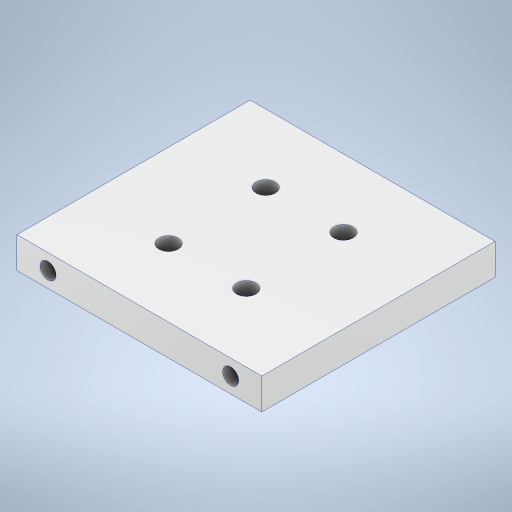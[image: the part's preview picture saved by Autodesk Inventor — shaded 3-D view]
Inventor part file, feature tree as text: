
AUTODESK INVENTOR PART (.ipt)
format: ipt  version: 2023 (Build 270158000, 158)  size: 278,016 bytes
history: native  units: mm
features: sketch x4, hole x3, other x3, extrude x1
ambient origin geometry x8: Origin, YZ Plane, XZ Plane, XY Plane, X Axis, Y Axis, Z Axis, Center Point
bodies: Body1 (feature_tree)
feature tree (11):
  extrude  "Extrusion2"  Depth=63.0mm
  hole  "Hole3"  [1 undecoded]
  hole  "Hole4"  [1 undecoded]
  hole  "Hole5"  [1 undecoded]
  sketch  "Sketch5"  dims[d43=53.25mm d68=63.0mm]
  sketch  "Sketch6"  dims[d69=60.0mm d70=8.0mm d71=0.0mm]
  sketch  "Sketch7"  dims[d72=20.0mm d74=25.0mm d75=20.0mm d77=20.0mm d80=63.0mm]
  sketch  "Sketch8"  dims[d81=60.0mm d82=21.5mm d83=17.5mm d84=5.0mm d85=6.0mm d86=4.0mm d87=2.0mm d88=90.0deg d89=5.0mm d90=20.594885mm d91=8.0mm d92=8.0mm d93=4.134mm d94=10.0mm d95=4.0mm d96=2.0mm d97=90.0deg d98=14.2mm d99=20.594885mm d100=4.134mm d101=10.0mm d102=4.0mm d103=2.0mm d104=90.0deg d105=14.2mm d106=20.594885mm d0=0.0mm d1=10.0mm d2=73.0mm]
  other  "Definição1"
  other  "Annotations"
  other  "Linear Dimension 1"
note: 3 required parameter values undecoded (feature->parameter linkage not recoverable at this tier; creation-order binding heuristic only, values carry confidence <= 0.55)
